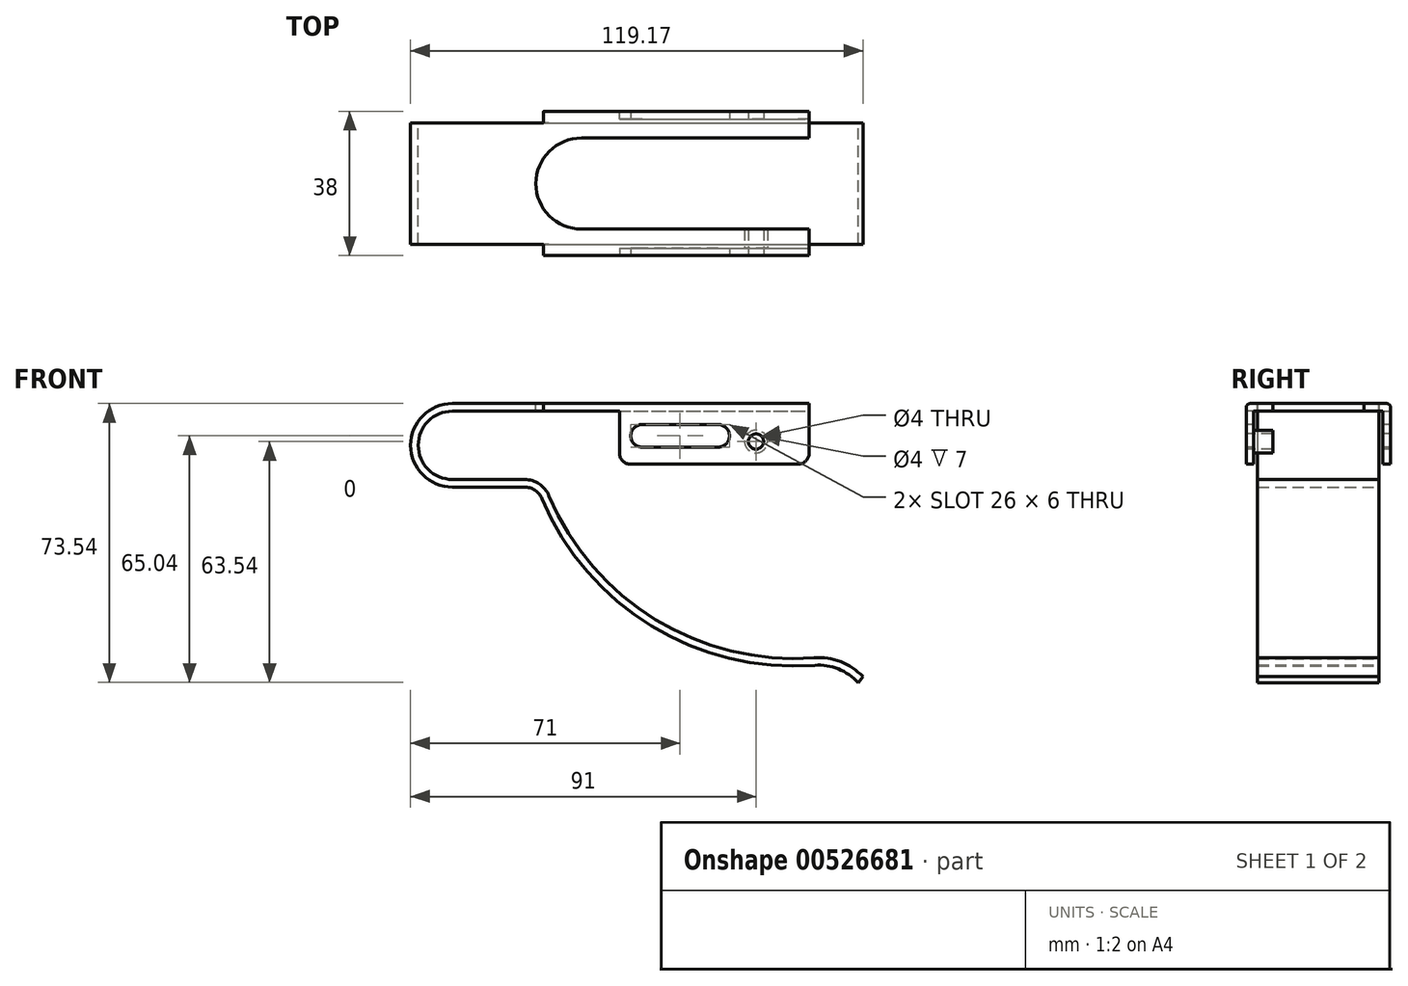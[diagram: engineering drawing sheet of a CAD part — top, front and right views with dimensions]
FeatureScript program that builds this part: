
annotation { "Feature Type Name" : "Feature", "Feature Type Description" : "" }
export const myFeature = defineFeature(function(context is Context, id is Id, definition is map)
    precondition{}
    {
        {
            var Q0;
            Q0=qCreatedBy(makeId("Front.planeOp"),FACE);
            var sketch = newSketch(context, id + "F0", { "sketchPlane" : qUnion([Q0])});
            skArc(sketch, "E0", {"start": v(0, 11) * mm, "mid": v(-11, 0) * mm, "end": v(0, -11) * mm});
            skLineSegment(sketch, "E1", {"start": v(0, -11) * mm, "end": v(19, -11) * mm});
            skArc(sketch, "E2", {"start": v(23.61, -14.06) * mm, "mid": v(52.44, -47.63) * mm, "end": v(95.45, -58) * mm});
            skLineSegment(sketch, "E3", {"start": v(0, 11) * mm, "end": v(94, 11) * mm});
            skArc(sketch, "E4", {"start": v(106.87, -62.54) * mm, "mid": v(101.69, -58.95) * mm, "end": v(95.45, -58) * mm});
            skPoint(sketch, "E5.visualSharp", {"position": v(22.4, -11) * mm});
            skArc(sketch, "E5.filletArc", {"start": v(23.61, -14.06) * mm, "mid": v(21.77, -11.84) * mm, "end": v(19, -11) * mm});
            skArc(sketch, "E6.0", {"start": v(108.17, -61) * mm, "mid": v(102.3, -57.04) * mm, "end": v(95.3, -56) * mm});
            skArc(sketch, "E6.1", {"start": v(25.45, -13.3) * mm, "mid": v(53.48, -45.92) * mm, "end": v(95.3, -56) * mm});
            skLineSegment(sketch, "E6.2", {"start": v(0, 9) * mm, "end": v(94, 9) * mm});
            skArc(sketch, "E6.3", {"start": v(0, 9) * mm, "mid": v(-9, 0) * mm, "end": v(0, -9) * mm});
            skLineSegment(sketch, "E6.4", {"start": v(0, -9) * mm, "end": v(19, -9) * mm});
            skArc(sketch, "E6.5", {"start": v(25.45, -13.3) * mm, "mid": v(22.88, -10.17) * mm, "end": v(19, -9) * mm});
            skLineSegment(sketch, "E7", {"start": v(94, 11) * mm, "end": v(94, 9) * mm});
            skLineSegment(sketch, "E8", {"start": v(108.17, -61) * mm, "end": v(106.87, -62.54) * mm});
            skLineSegment(sketch, "E9", {"start": v(112.4, -61) * mm, "end": v(117.08, -61) * mm});
            skSolve(sketch);
        }
        {
            var Q0;
            Q0=qSketchRegion(id+"F0",true);
            extrude(context, id + "F1", {"entities" : qUnion([Q0]), "offsetDistance" : 25 * mm, "depth" : 16 * mm});
        }
        {
            var Q0;
            Q0=makeQuery(id+"F1.opExtrude","SWEPT_FACE",FACE,{"disambiguationData":[OSD([sQuery(id+"F0.wireOp",EDGE,"E3")])]});
            var sketch = newSketch(context, id + "F2", { "sketchPlane" : qUnion([Q0])});
            skLineSegment(sketch, "E10.bottom", {"start": v(24, -16) * mm, "end": v(94, -16) * mm});
            skLineSegment(sketch, "E10.top", {"start": v(24, -19) * mm, "end": v(94, -19) * mm});
            skLineSegment(sketch, "E10.left", {"start": v(24, -16) * mm, "end": v(24, -19) * mm});
            skLineSegment(sketch, "E10.right", {"start": v(94, -16) * mm, "end": v(94, -19) * mm});
            skSolve(sketch);
        }
        {
            var Q0;
            Q0=qSketchRegion(id+"F2",true);
            extrude(context, id + "F3", {"entities" : qUnion([Q0]), "operationType" : NewBodyOperationType.ADD, "oppositeDirection" : true, "offsetDistance" : 25 * mm, "depth" : 2 * mm});
        }
        {
            var Q0;
            Q0=makeQuery(id+"F3.opExtrude","SWEPT_FACE",FACE,{"disambiguationData":[OSD([sQuery(id+"F2.wireOp",EDGE,"E10.top")])]});
            var sketch = newSketch(context, id + "F4", { "sketchPlane" : qUnion([Q0])});
            skLineSegment(sketch, "E11.bottom", {"start": v(24, 9) * mm, "end": v(94, 9) * mm});
            skLineSegment(sketch, "E11.top", {"start": v(44, -5) * mm, "end": v(94, -5) * mm});
            skLineSegment(sketch, "E11.left", {"start": v(44, 9) * mm, "end": v(44, -5) * mm});
            skLineSegment(sketch, "E11.right", {"start": v(94, 9) * mm, "end": v(94, -5) * mm});
            skSolve(sketch);
        }
        {
            var Q0;
            Q0=qSketchRegion(id+"F4",true);
            extrude(context, id + "F5", {"entities" : qUnion([Q0]), "operationType" : NewBodyOperationType.ADD, "oppositeDirection" : true, "depth" : 2 * mm});
        }
        {
            var Q0;
            Q0=makeQuery(id+"F3.opExtrude","CAP_EDGE",EDGE,{"disambiguationData":[OSD([sQuery(id+"F2.wireOp",EDGE,"E10.top")])],"isStart":true});
            var Q1;
            Q1=makeQuery(id+"F5.opExtrude","CAP_EDGE",EDGE,{"disambiguationData":[OSD([sQuery(id+"F4.wireOp",EDGE,"E11.bottom")])],"isStart":false});
            fillet(context, id + "F6", {"entities" : qUnion([Q0, Q1]), "radius" : 1 * mm, "tangentPropagation" : true, "allowEdgeOverflow" : false});
        }
        {
            var Q0;
            Q0=makeQuery(id+"F1.opExtrude","SWEPT_BODY",BODY,{"disambiguationData":[OSD([sQuery(id+"F0.wireOp",EDGE,"E0"),sQuery(id+"F0.wireOp",EDGE,"E1"),sQuery(id+"F0.wireOp",EDGE,"E2"),sQuery(id+"F0.wireOp",EDGE,"E3"),sQuery(id+"F0.wireOp",EDGE,"E4"),sQuery(id+"F0.wireOp",EDGE,"E5.filletArc"),sQuery(id+"F0.wireOp",EDGE,"E6.0"),sQuery(id+"F0.wireOp",EDGE,"E6.1"),sQuery(id+"F0.wireOp",EDGE,"E6.2"),sQuery(id+"F0.wireOp",EDGE,"E6.3"),sQuery(id+"F0.wireOp",EDGE,"E6.4"),sQuery(id+"F0.wireOp",EDGE,"E6.5"),sQuery(id+"F0.wireOp",EDGE,"E7"),sQuery(id+"F0.wireOp",EDGE,"E8")])]});
            var Q1;
            Q1=qCreatedBy(makeId("Front.planeOp"),FACE);
            mirror(context, id + "F7", {"operationType" : NewBodyOperationType.ADD, "entities" : qUnion([Q0]), "mirrorPlane" : qUnion([Q1])});
        }
        {
            var Q0;
            {var subQ0=makeQuery(id+"F3.boolean.opBoolean","MERGE",FACE,{"derivedFrom":[makeQuery(id+"F1.opExtrude","SWEPT_FACE",FACE,{"disambiguationData":[OSD([sQuery(id+"F0.wireOp",EDGE,"E3")])]}),makeQuery(id+"F3.opExtrude","CAP_FACE",FACE,{"disambiguationData":[OSD([sQuery(id+"F2.wireOp",EDGE,"E10.bottom"),sQuery(id+"F2.wireOp",EDGE,"E10.top"),sQuery(id+"F2.wireOp",EDGE,"E10.left"),sQuery(id+"F2.wireOp",EDGE,"E10.right")])],"isStart":true})]});Q0=makeQuery(id+"F7.boolean.opBoolean","MERGE",FACE,{"derivedFrom":[subQ0,makeQuery(id+"F7.opPattern","COPY",FACE,{"derivedFrom":subQ0,"instanceName":"1"})]});}
            var sketch = newSketch(context, id + "F8", { "sketchPlane" : qUnion([Q0])});
            skArc(sketch, "E12", {"start": v(34, 12) * mm, "mid": v(22, 0) * mm, "end": v(34, -12) * mm});
            skLineSegment(sketch, "E13", {"start": v(34, -12) * mm, "end": v(94, -12) * mm});
            skLineSegment(sketch, "E14", {"start": v(34, 12) * mm, "end": v(94, 12) * mm});
            skLineSegment(sketch, "E15", {"start": v(94, 12) * mm, "end": v(94, -12) * mm});
            skSolve(sketch);
        }
        {
            var Q0;
            Q0=qSketchRegion(id+"F8",true);
            extrude(context, id + "F9", {"entities" : qUnion([Q0]), "operationType" : NewBodyOperationType.REMOVE, "oppositeDirection" : true, "offsetDistance" : 25 * mm, "depth" : 4 * mm});
        }
        {
            var Q0;
            Q0=makeQuery(id+"F5.boolean.opBoolean","MERGE",FACE,{"derivedFrom":[makeQuery(id+"F3.opExtrude","SWEPT_FACE",FACE,{"disambiguationData":[OSD([sQuery(id+"F2.wireOp",EDGE,"E10.top")])]}),makeQuery(id+"F5.opExtrude","CAP_FACE",FACE,{"disambiguationData":[OSD([sQuery(id+"F4.wireOp",EDGE,"E11.bottom"),sQuery(id+"F4.wireOp",EDGE,"E11.top"),sQuery(id+"F4.wireOp",EDGE,"E11.left"),sQuery(id+"F4.wireOp",EDGE,"E11.right")])],"isStart":true})]});
            var sketch = newSketch(context, id + "F10", { "sketchPlane" : qUnion([Q0])});
            skLineSegment(sketch, "E16", {"start": v(70, 2.5) * mm, "end": v(50, 2.5) * mm});
            skPoint(sketch, "E16.startSnap0", {"position": v(94, 2.5) * mm});
            skArc(sketch, "E17.0.startCap", {"start": v(70, 5.5) * mm, "mid": v(73, 2.5) * mm, "end": v(70, -0.5) * mm});
            skArc(sketch, "E17.0.endCap", {"start": v(50, -0.5) * mm, "mid": v(47, 2.5) * mm, "end": v(50, 5.5) * mm});
            skLineSegment(sketch, "E17.0.left", {"start": v(70, -0.5) * mm, "end": v(50, -0.5) * mm});
            skLineSegment(sketch, "E17.0.right", {"start": v(70, 5.5) * mm, "end": v(50, 5.5) * mm});
            skSolve(sketch);
        }
        {
            var Q0;
            Q0=qSketchRegion(id+"F10",true);
            extrude(context, id + "F11", {"entities" : qUnion([Q0]), "operationType" : NewBodyOperationType.REMOVE, "endBound" : BoundingType.THROUGH_ALL, "oppositeDirection" : true, "depth" : 25 * mm});
        }
        {
            var Q0;
            Q0=makeQuery(id+"F5.boolean.opBoolean","MERGE",FACE,{"derivedFrom":[makeQuery(id+"F3.opExtrude","SWEPT_FACE",FACE,{"disambiguationData":[OSD([sQuery(id+"F2.wireOp",EDGE,"E10.top")])]}),makeQuery(id+"F5.opExtrude","CAP_FACE",FACE,{"disambiguationData":[OSD([sQuery(id+"F4.wireOp",EDGE,"E11.bottom"),sQuery(id+"F4.wireOp",EDGE,"E11.top"),sQuery(id+"F4.wireOp",EDGE,"E11.left"),sQuery(id+"F4.wireOp",EDGE,"E11.right")])],"isStart":true})]});
            var sketch = newSketch(context, id + "F12", { "sketchPlane" : qUnion([Q0])});
            skPoint(sketch, "E18", {"position": v(80, 1) * mm});
            skSolve(sketch);
        }
        {
            var Q0;
            Q0=sQuery(id+"F12.wireOp",VERTEX,"E18");
            var Q1;
            Q1=makeQuery(id+"F1.opExtrude","SWEPT_BODY",BODY,{"disambiguationData":[OSD([sQuery(id+"F0.wireOp",EDGE,"E0"),sQuery(id+"F0.wireOp",EDGE,"E1"),sQuery(id+"F0.wireOp",EDGE,"E2"),sQuery(id+"F0.wireOp",EDGE,"E3"),sQuery(id+"F0.wireOp",EDGE,"E4"),sQuery(id+"F0.wireOp",EDGE,"E5.filletArc"),sQuery(id+"F0.wireOp",EDGE,"E6.0"),sQuery(id+"F0.wireOp",EDGE,"E6.1"),sQuery(id+"F0.wireOp",EDGE,"E6.2"),sQuery(id+"F0.wireOp",EDGE,"E6.3"),sQuery(id+"F0.wireOp",EDGE,"E6.4"),sQuery(id+"F0.wireOp",EDGE,"E6.5"),sQuery(id+"F0.wireOp",EDGE,"E7"),sQuery(id+"F0.wireOp",EDGE,"E8")])]});
            hole(context, id + "F13", {"style" : HoleStyle.SIMPLE, "endStyle" : HoleEndStyle.THROUGH, "holeDiameter" : 4 * mm, "isTappedThrough" : true, "tappedDepth" : 12 * mm, "tapClearance" : 3, "locations" : qUnion([Q0]), "scope" : qUnion([Q1])});
        }
        {
            var Q0;
            Q0=makeQuery(id+"F5.opExtrude","CAP_FACE",FACE,{"disambiguationData":[OSD([sQuery(id+"F4.wireOp",EDGE,"E11.bottom"),sQuery(id+"F4.wireOp",EDGE,"E11.top"),sQuery(id+"F4.wireOp",EDGE,"E11.left"),sQuery(id+"F4.wireOp",EDGE,"E11.right")])],"isStart":false});
            var sketch = newSketch(context, id + "F14", { "sketchPlane" : qUnion([Q0])});
            skCircle(sketch, "E19.0", {"center": v(-80, 1) * mm, "radius": 2 * mm});
            skCircle(sketch, "E20.0", {"center": v(-80, 1) * mm, "radius": 3 * mm});
            skSolve(sketch);
        }
        {
            var Q0;
            Q0=qSketchRegion(id+"F14",true);
            extrude(context, id + "F15", {"entities" : qUnion([Q0]), "operationType" : NewBodyOperationType.ADD, "depth" : 5 * mm});
        }
        {
            var Q0;
            Q0=makeQuery(id+"F7.opPattern","COPY",EDGE,{"derivedFrom":makeQuery(id+"F5.opExtrude","SWEPT_EDGE",EDGE,{"disambiguationData":[OSD([sQuery(id+"F4.wireOp",EDGE,"E11.top"),sQuery(id+"F4.wireOp",EDGE,"E11.right")])]}),"instanceName":"1"});
            var Q1;
            Q1=makeQuery(id+"F7.opPattern","COPY",EDGE,{"derivedFrom":makeQuery(id+"F5.opExtrude","SWEPT_EDGE",EDGE,{"disambiguationData":[OSD([sQuery(id+"F4.wireOp",EDGE,"E11.top"),sQuery(id+"F4.wireOp",EDGE,"E11.left")])]}),"instanceName":"1"});
            var Q2;
            Q2=makeQuery(id+"F5.opExtrude","SWEPT_EDGE",EDGE,{"disambiguationData":[OSD([sQuery(id+"F4.wireOp",EDGE,"E11.top"),sQuery(id+"F4.wireOp",EDGE,"E11.right")])]});
            var Q3;
            Q3=makeQuery(id+"F5.opExtrude","SWEPT_EDGE",EDGE,{"disambiguationData":[OSD([sQuery(id+"F4.wireOp",EDGE,"E11.top"),sQuery(id+"F4.wireOp",EDGE,"E11.left")])]});
            fillet(context, id + "F16", {"entities" : qUnion([Q0, Q1, Q2, Q3]), "radius" : 3 * mm, "tangentPropagation" : true, "allowEdgeOverflow" : false});
        }
    });
